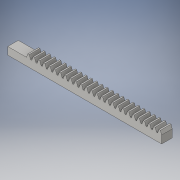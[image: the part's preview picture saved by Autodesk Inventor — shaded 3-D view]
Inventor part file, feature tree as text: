
AUTODESK INVENTOR PART (.ipt)
format: ipt  version: 2016 (Build 200138000, 138)  size: 279,552 bytes
history: native  units: in
note: dims shown in document units (in); Inventor stores cm internally (conversion verified against a paired STEP export)
features: extrude x1, sketch x1
ambient origin geometry x8: Origin, YZ Plane, XZ Plane, XY Plane, X Axis, Y Axis, Z Axis, Center Point
bodies: Solid1 (feature_tree)
feature tree (2):
  extrude  "Extrusion1"  Depth=0.5in
  sketch  "Sketch1"  dims[d0=0.5in d1=0.0in d4=0.0245in d5=0.0122in]
